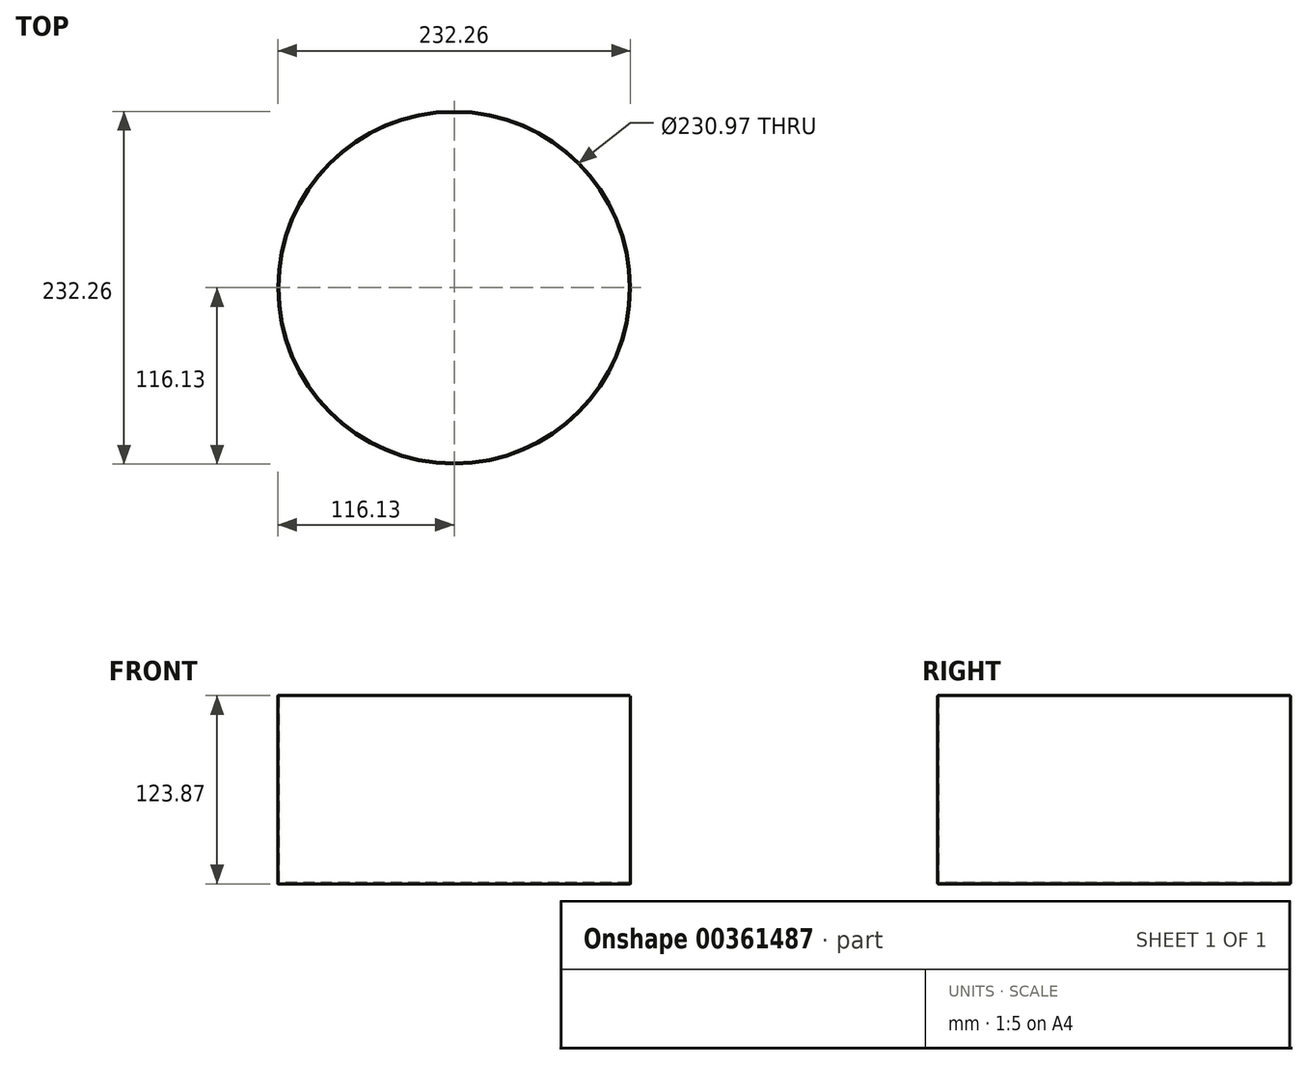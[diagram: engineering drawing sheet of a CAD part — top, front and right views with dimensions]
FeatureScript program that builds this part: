
annotation { "Feature Type Name" : "Feature", "Feature Type Description" : "" }
export const myFeature = defineFeature(function(context is Context, id is Id, definition is map)
    precondition{}
    {
        {
            var Q0;
            Q0=qCreatedBy(makeId("Top.planeOp"),FACE);
            var sketch = newSketch(context, id + "F0", { "sketchPlane" : qUnion([Q0])});
            skCircle(sketch, "E0", {"center": v(0, 0) * mm, "radius": 116.13 * mm});
            skSolve(sketch);
        }
        {
            var Q0;
            Q0=makeQuery(id+"F0.imprint","IMPRINT",FACE,{"disambiguationData":[TD([[makeQuery(id+"F0.imprint","IMPRINT",EDGE,{"derivedFrom":sQuery(id+"F0.wireOp",EDGE,"E0")}),1.0]])]});
            extrude(context, id + "F1", {"entities" : qUnion([Q0]), "depth" : 16 * 7.74 * mm});
        }
        {
            var Q0;
            Q0=makeQuery(id+"F1.opExtrude","CAP_FACE",FACE,{"disambiguationData":[OSD([sQuery(id+"F0.wireOp",EDGE,"E0")])],"isStart":false});
            shell(context, id + "F2", {"entities" : qUnion([Q0]), "thickness" : 0.65 * mm});
        }
        {
            var Q0;
            Q0=makeQuery(id+"F1.opExtrude","CAP_FACE",FACE,{"disambiguationData":[OSD([sQuery(id+"F0.wireOp",EDGE,"E0")])],"isStart":false});
            fillet(context, id + "F3", {"entities" : qUnion([Q0]), "radius" : 0.32 * mm, "tangentPropagation" : true, "allowEdgeOverflow" : false});
        }
        {
            var Q0;
            {var subQ0=sQuery(id+"F0.wireOp",EDGE,"E0");Q0=makeQuery(id+"F2.opShell","OFFSET_EDGE",EDGE,{"disambiguationData":[OSD([subQ0]),TDD([makeQuery(id+"F1.opExtrude","CAP_EDGE",EDGE,{"disambiguationData":[OSD([subQ0])],"isStart":true})])]});}
            fillet(context, id + "F4", {"entities" : qUnion([Q0]), "radius" : 0.32 * mm, "tangentPropagation" : true, "allowEdgeOverflow" : false});
        }
        {
            var Q0;
            Q0=makeQuery(id+"F1.opExtrude","CAP_EDGE",EDGE,{"disambiguationData":[OSD([sQuery(id+"F0.wireOp",EDGE,"E0")])],"isStart":true});
            fillet(context, id + "F5", {"entities" : qUnion([Q0]), "radius" : 0.32 * mm, "tangentPropagation" : true, "allowEdgeOverflow" : false});
        }
    });
